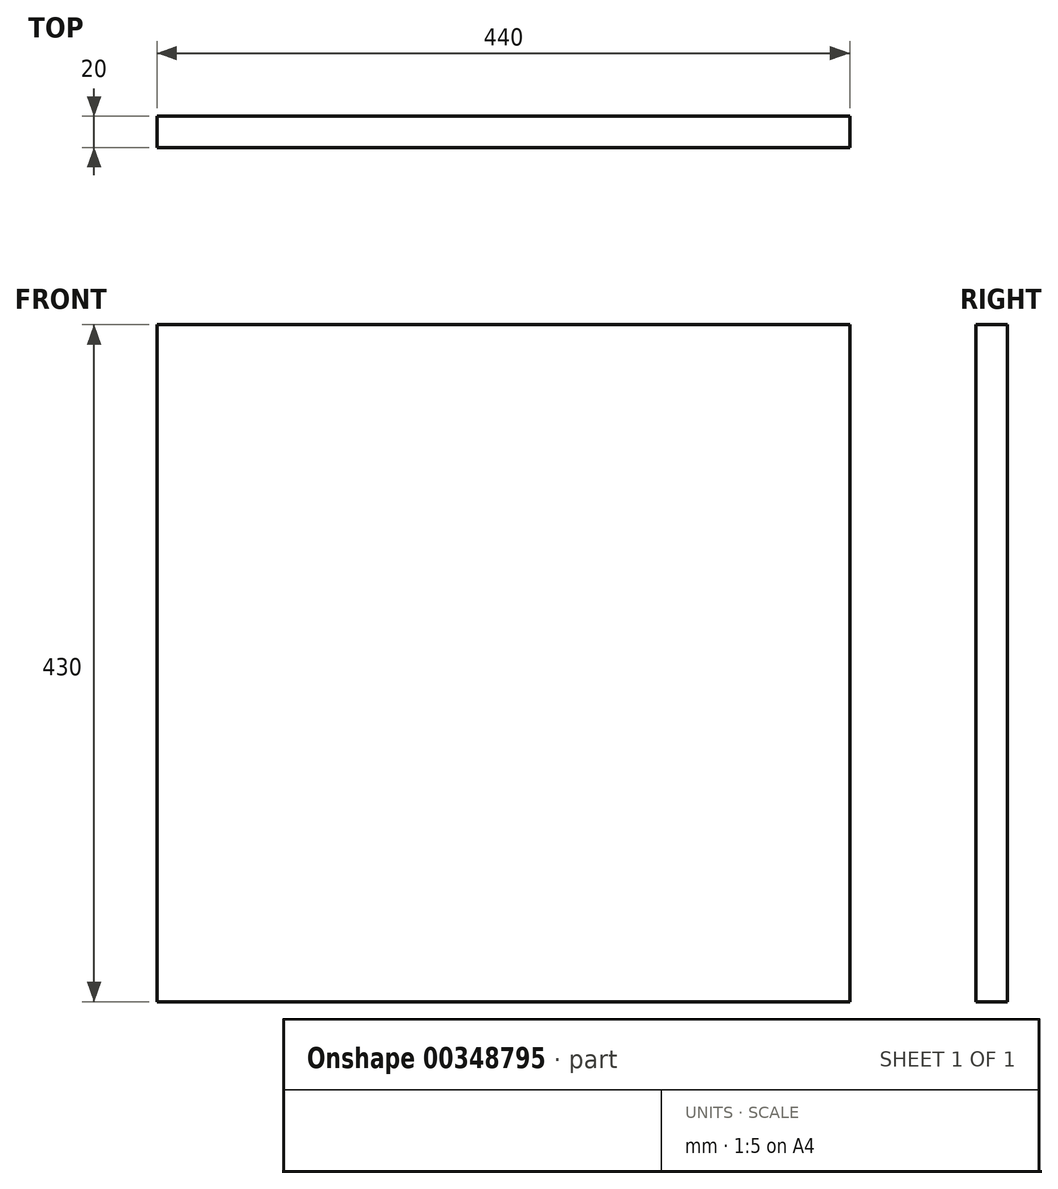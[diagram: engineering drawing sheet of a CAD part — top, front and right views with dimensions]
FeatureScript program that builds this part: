
annotation { "Feature Type Name" : "Feature", "Feature Type Description" : "" }
export const myFeature = defineFeature(function(context is Context, id is Id, definition is map)
    precondition{}
    {
        {
            var Q0;
            Q0=qCreatedBy(makeId("Front.planeOp"),FACE);
            var sketch = newSketch(context, id + "F0", { "sketchPlane" : qUnion([Q0])});
            skLineSegment(sketch, "E0.bottom", {"start": v(-440, -430) * mm, "end": v(0, -430) * mm});
            skLineSegment(sketch, "E0.top", {"start": v(-440, 0) * mm, "end": v(0, 0) * mm});
            skLineSegment(sketch, "E0.left", {"start": v(-440, -430) * mm, "end": v(-440, 0) * mm});
            skLineSegment(sketch, "E0.right", {"start": v(0, -430) * mm, "end": v(0, 0) * mm});
            skSolve(sketch);
        }
        {
            var Q0;
            Q0=qSketchRegion(id+"F0",true);
            extrude(context, id + "F1", {"entities" : qUnion([Q0]), "depth" : 20 * mm});
        }
    });
